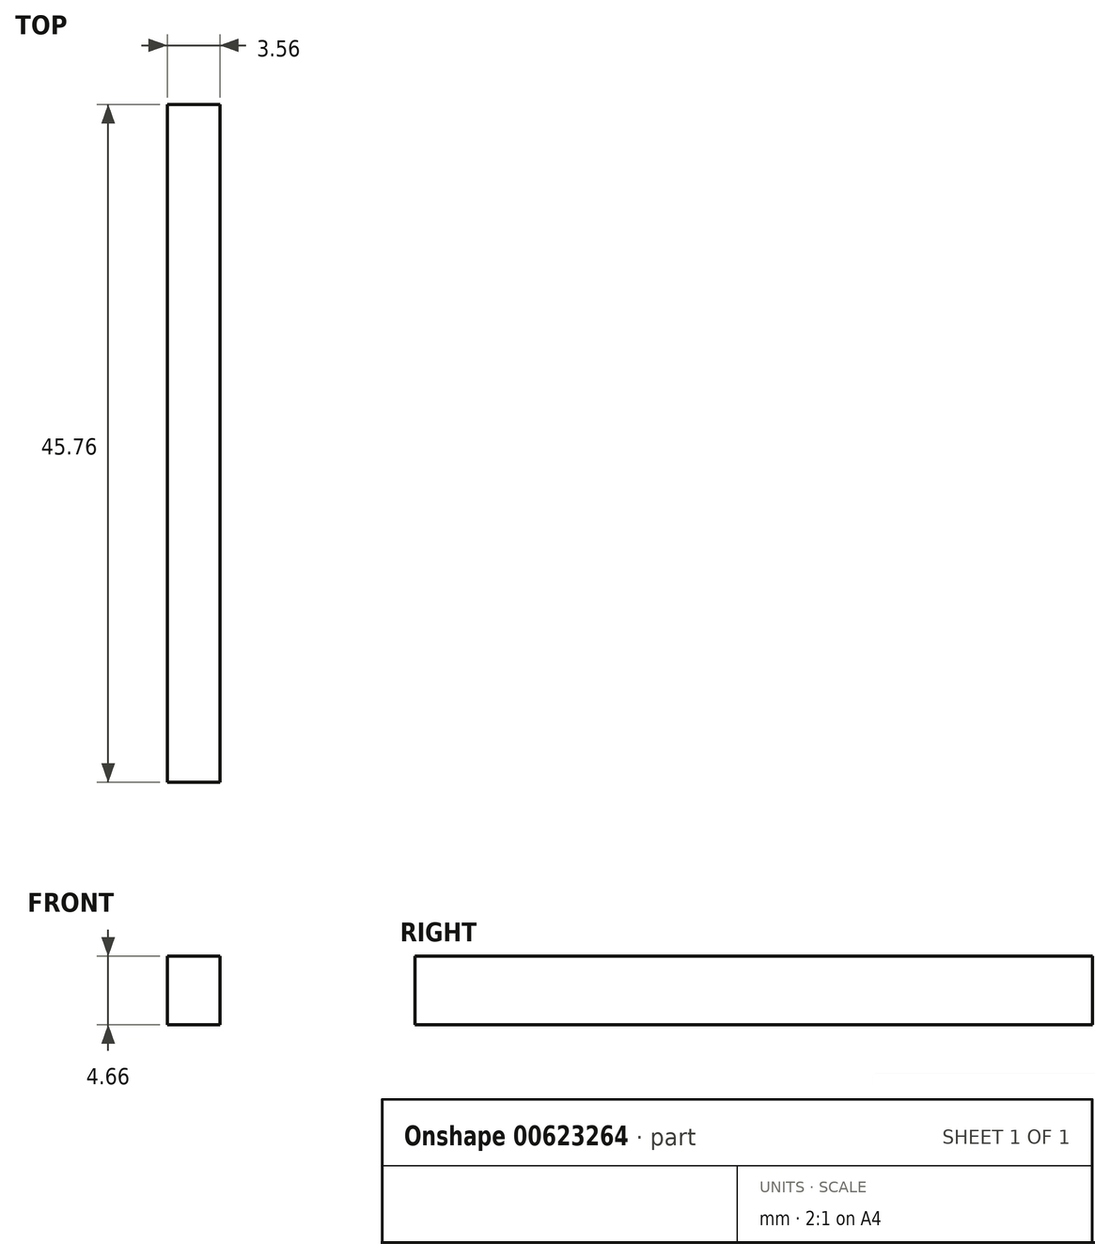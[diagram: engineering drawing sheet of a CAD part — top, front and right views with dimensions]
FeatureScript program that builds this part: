
annotation { "Feature Type Name" : "Feature", "Feature Type Description" : "" }
export const myFeature = defineFeature(function(context is Context, id is Id, definition is map)
    precondition{}
    {
        {
            var Q0;
            Q0=qCreatedBy(makeId("Right.planeOp"),FACE);
            var sketch = newSketch(context, id + "F0", { "sketchPlane" : qUnion([Q0])});
            skLineSegment(sketch, "E0.bottom", {"start": v(-22.88, -2.33) * mm, "end": v(22.88, -2.33) * mm});
            skLineSegment(sketch, "E0.top", {"start": v(-22.88, 2.33) * mm, "end": v(22.88, 2.33) * mm});
            skLineSegment(sketch, "E0.left", {"start": v(-22.88, -2.33) * mm, "end": v(-22.88, 2.33) * mm});
            skLineSegment(sketch, "E0.right", {"start": v(22.88, -2.33) * mm, "end": v(22.88, 2.33) * mm});
            skPoint(sketch, "E0.middle", {"position": v(0, 0) * mm});
            skSolve(sketch);
        }
        {
            var Q0;
            Q0 = qSketchRegion(id + "F0", true);
            extrude(context, id + "F1", {"entities" : qUnion([Q0]), "depth" : 3.56 * mm, "offsetDistance" : 25.4 * mm});
        }
    });
